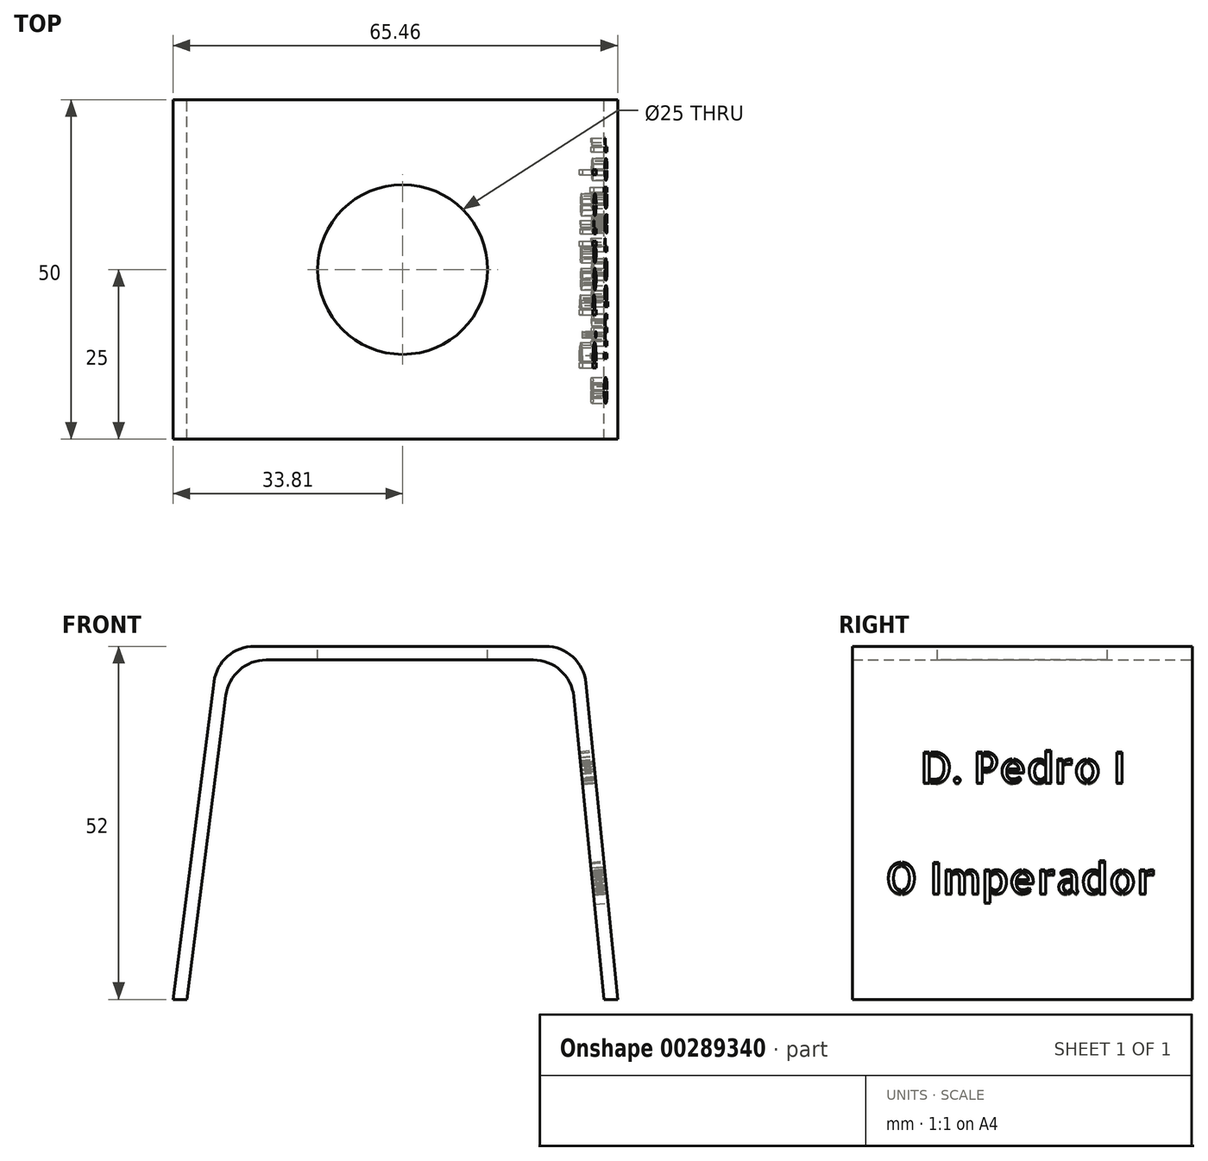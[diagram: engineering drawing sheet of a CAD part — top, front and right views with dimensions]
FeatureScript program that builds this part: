
annotation { "Feature Type Name" : "Feature", "Feature Type Description" : "" }
export const myFeature = defineFeature(function(context is Context, id is Id, definition is map)
    precondition{}
    {
        {
            var Q0;
            Q0=qCreatedBy(makeId("Front.planeOp"),FACE);
            var sketch = newSketch(context, id + "F0", { "sketchPlane" : qUnion([Q0])});
            skPoint(sketch, "E0", {"position": v(0, 0) * mm});
            skLineSegment(sketch, "E1", {"start": v(-31.8, 0) * mm, "end": v(-25.36, 50) * mm});
            skLineSegment(sketch, "E2", {"start": v(24.64, 50) * mm, "end": v(29.64, 0) * mm});
            skLineSegment(sketch, "E3", {"start": v(-25.36, 50) * mm, "end": v(24.64, 50) * mm});
            skLineSegment(sketch, "E4.0", {"start": v(26.45, 52) * mm, "end": v(31.65, 0) * mm});
            skLineSegment(sketch, "E4.1", {"start": v(-27.11, 52) * mm, "end": v(26.45, 52) * mm});
            skLineSegment(sketch, "E4.2", {"start": v(-33.81, 0) * mm, "end": v(-27.11, 52) * mm});
            skLineSegment(sketch, "E5", {"start": v(-33.81, 0) * mm, "end": v(-31.8, 0) * mm});
            skLineSegment(sketch, "E6", {"start": v(29.64, 0) * mm, "end": v(31.65, 0) * mm});
            skSolve(sketch);
        }
        {
            var Q0;
            Q0=makeQuery(id+"F0.imprint","IMPRINT",FACE,{"disambiguationData":[TD([[makeQuery(id+"F0.imprint","IMPRINT",EDGE,{"derivedFrom":sQuery(id+"F0.wireOp",EDGE,"E1")}),1.0]])]});
            var Q1;
            Q1=sQuery(id+"F0.wireOp",EDGE,"E4.2");
            var Q2;
            Q2=sQuery(id+"F0.wireOp",EDGE,"E1");
            extrude(context, id + "F1", {"entities" : qUnion([Q0]), "surfaceEntities" : qUnion([Q1, Q2]), "depth" : 50 * mm});
        }
        {
            var Q0;
            Q0=makeQuery(id+"F1.opExtrude","SWEPT_EDGE",EDGE,{"disambiguationData":[OSD([sQuery(id+"F0.wireOp",EDGE,"E4.0"),sQuery(id+"F0.wireOp",EDGE,"E4.1")])]});
            var Q1;
            Q1=makeQuery(id+"F1.opExtrude","SWEPT_EDGE",EDGE,{"disambiguationData":[OSD([sQuery(id+"F0.wireOp",EDGE,"E4.1"),sQuery(id+"F0.wireOp",EDGE,"E4.2")])]});
            var Q2;
            Q2=makeQuery(id+"F1.opExtrude","SWEPT_EDGE",EDGE,{"disambiguationData":[OSD([sQuery(id+"F0.wireOp",EDGE,"E1"),sQuery(id+"F0.wireOp",EDGE,"E3")])]});
            var Q3;
            Q3=makeQuery(id+"F1.opExtrude","SWEPT_EDGE",EDGE,{"disambiguationData":[OSD([sQuery(id+"F0.wireOp",EDGE,"E2"),sQuery(id+"F0.wireOp",EDGE,"E3")])]});
            fillet(context, id + "F2", {"entities" : qUnion([Q0, Q1, Q2, Q3]), "radius" : 6 * mm, "tangentPropagation" : true});
        }
        {
            var Q0;
            Q0=makeQuery(id+"F1.opExtrude","SWEPT_FACE",FACE,{"disambiguationData":[OSD([sQuery(id+"F0.wireOp",EDGE,"E4.0")])]});
            var sketch = newSketch(context, id + "F3", { "sketchPlane" : qUnion([Q0])});
            skText(sketch, "E7", { "text": "   D. Pedro I\n\nO Imperador", "fontName": "AllertaStencil-Regular.ttf"});
            const initialGuessF3  = {"E7": [-0.04521, 0.02888, 1, 0, 0.00461]};
            skSetInitialGuess(sketch, initialGuessF3);
            skSolve(sketch);
        }
        {
            var Q0;
            Q0=qSketchRegion(id+"F3",true);
            var Q1;
            Q1=makeQuery(id+"F3.imprint","IMPRINT",FACE,{"disambiguationData":[TD([[makeQuery(id+"F3.imprint","IMPRINT",EDGE,{"derivedFrom":sQuery(id+"F3.wireOp",EDGE,"E7.sketch_text.stroke-38")}),-1.0]])]});
            var Q2;
            Q2=makeQuery(id+"F3.imprint","IMPRINT",FACE,{"disambiguationData":[TD([[makeQuery(id+"F3.imprint","IMPRINT",EDGE,{"derivedFrom":sQuery(id+"F3.wireOp",EDGE,"E7.sketch_text.stroke-34")}),-1.0]])]});
            var Q3;
            Q3=makeQuery(id+"F3.imprint","IMPRINT",FACE,{"disambiguationData":[TD([[makeQuery(id+"F3.imprint","IMPRINT",EDGE,{"derivedFrom":sQuery(id+"F3.wireOp",EDGE,"E7.sketch_text.stroke-26")}),-1.0]])]});
            var Q4;
            Q4=makeQuery(id+"F3.imprint","IMPRINT",FACE,{"disambiguationData":[TD([[makeQuery(id+"F3.imprint","IMPRINT",EDGE,{"derivedFrom":sQuery(id+"F3.wireOp",EDGE,"E7.sketch_text.stroke-4")}),-1.0]])]});
            var Q5;
            Q5=makeQuery(id+"F3.imprint","IMPRINT",FACE,{"disambiguationData":[TD([[makeQuery(id+"F3.imprint","IMPRINT",EDGE,{"derivedFrom":sQuery(id+"F3.wireOp",EDGE,"E7.sketch_text.stroke-0")}),-1.0]])]});
            var Q6;
            Q6=makeQuery(id+"F3.imprint","IMPRINT",FACE,{"disambiguationData":[TD([[makeQuery(id+"F3.imprint","IMPRINT",EDGE,{"derivedFrom":sQuery(id+"F3.wireOp",EDGE,"E7.sketch_text.stroke-177")}),-1.0]])]});
            var Q7;
            Q7=makeQuery(id+"F3.imprint","IMPRINT",FACE,{"disambiguationData":[TD([[makeQuery(id+"F3.imprint","IMPRINT",EDGE,{"derivedFrom":sQuery(id+"F3.wireOp",EDGE,"E7.sketch_text.stroke-193")}),-1.0]])]});
            var Q8;
            Q8=makeQuery(id+"F3.imprint","IMPRINT",FACE,{"disambiguationData":[TD([[makeQuery(id+"F3.imprint","IMPRINT",EDGE,{"derivedFrom":sQuery(id+"F3.wireOp",EDGE,"E7.sketch_text.stroke-327")}),-1.0]])]});
            var Q9;
            Q9=makeQuery(id+"F3.imprint","IMPRINT",FACE,{"disambiguationData":[TD([[makeQuery(id+"F3.imprint","IMPRINT",EDGE,{"derivedFrom":sQuery(id+"F3.wireOp",EDGE,"E7.sketch_text.stroke-320")}),-1.0]])]});
            var Q10;
            Q10=makeQuery(id+"F3.imprint","IMPRINT",FACE,{"disambiguationData":[TD([[makeQuery(id+"F3.imprint","IMPRINT",EDGE,{"derivedFrom":sQuery(id+"F3.wireOp",EDGE,"E7.sketch_text.stroke-296")}),-1.0]])]});
            var Q11;
            Q11=makeQuery(id+"F3.imprint","IMPRINT",FACE,{"disambiguationData":[TD([[makeQuery(id+"F3.imprint","IMPRINT",EDGE,{"derivedFrom":sQuery(id+"F3.wireOp",EDGE,"E7.sketch_text.stroke-97")}),-1.0]])]});
            var Q12;
            Q12=makeQuery(id+"F3.imprint","IMPRINT",FACE,{"disambiguationData":[TD([[makeQuery(id+"F3.imprint","IMPRINT",EDGE,{"derivedFrom":sQuery(id+"F3.wireOp",EDGE,"E7.sketch_text.stroke-257")}),-1.0]])]});
            var Q13;
            Q13=makeQuery(id+"F3.imprint","IMPRINT",FACE,{"disambiguationData":[TD([[makeQuery(id+"F3.imprint","IMPRINT",EDGE,{"derivedFrom":sQuery(id+"F3.wireOp",EDGE,"E7.sketch_text.stroke-252")}),-1.0]])]});
            var Q14;
            Q14=makeQuery(id+"F3.imprint","IMPRINT",FACE,{"disambiguationData":[TD([[makeQuery(id+"F3.imprint","IMPRINT",EDGE,{"derivedFrom":sQuery(id+"F3.wireOp",EDGE,"E7.sketch_text.stroke-157")}),-1.0]])]});
            var Q15;
            Q15=makeQuery(id+"F3.imprint","IMPRINT",FACE,{"disambiguationData":[TD([[makeQuery(id+"F3.imprint","IMPRINT",EDGE,{"derivedFrom":sQuery(id+"F3.wireOp",EDGE,"E7.sketch_text.stroke-60")}),-1.0]])]});
            var Q16;
            Q16=makeQuery(id+"F3.imprint","IMPRINT",FACE,{"disambiguationData":[TD([[makeQuery(id+"F3.imprint","IMPRINT",EDGE,{"derivedFrom":sQuery(id+"F3.wireOp",EDGE,"E7.sketch_text.stroke-234")}),-1.0]])]});
            var Q17;
            Q17=makeQuery(id+"F3.imprint","IMPRINT",FACE,{"disambiguationData":[TD([[makeQuery(id+"F3.imprint","IMPRINT",EDGE,{"derivedFrom":sQuery(id+"F3.wireOp",EDGE,"E7.sketch_text.stroke-141")}),-1.0]])]});
            var Q18;
            Q18=makeQuery(id+"F3.imprint","IMPRINT",FACE,{"disambiguationData":[TD([[makeQuery(id+"F3.imprint","IMPRINT",EDGE,{"derivedFrom":sQuery(id+"F3.wireOp",EDGE,"E7.sketch_text.stroke-218")}),-1.0]])]});
            var Q19;
            Q19=makeQuery(id+"F3.imprint","IMPRINT",FACE,{"disambiguationData":[TD([[makeQuery(id+"F3.imprint","IMPRINT",EDGE,{"derivedFrom":sQuery(id+"F3.wireOp",EDGE,"E7.sketch_text.stroke-458")}),-1.0]])]});
            var Q20;
            Q20=makeQuery(id+"F3.imprint","IMPRINT",FACE,{"disambiguationData":[TD([[makeQuery(id+"F3.imprint","IMPRINT",EDGE,{"derivedFrom":sQuery(id+"F3.wireOp",EDGE,"E7.sketch_text.stroke-394")}),-1.0]])]});
            var Q21;
            Q21=makeQuery(id+"F3.imprint","IMPRINT",FACE,{"disambiguationData":[TD([[makeQuery(id+"F3.imprint","IMPRINT",EDGE,{"derivedFrom":sQuery(id+"F3.wireOp",EDGE,"E7.sketch_text.stroke-435")}),-1.0]])]});
            var Q22;
            Q22=makeQuery(id+"F3.imprint","IMPRINT",FACE,{"disambiguationData":[TD([[makeQuery(id+"F3.imprint","IMPRINT",EDGE,{"derivedFrom":sQuery(id+"F3.wireOp",EDGE,"E7.sketch_text.stroke-73")}),-1.0]])]});
            var Q23;
            Q23=makeQuery(id+"F3.imprint","IMPRINT",FACE,{"disambiguationData":[TD([[makeQuery(id+"F3.imprint","IMPRINT",EDGE,{"derivedFrom":sQuery(id+"F3.wireOp",EDGE,"E7.sketch_text.stroke-389")}),-1.0]])]});
            var Q24;
            Q24=makeQuery(id+"F3.imprint","IMPRINT",FACE,{"disambiguationData":[TD([[makeQuery(id+"F3.imprint","IMPRINT",EDGE,{"derivedFrom":sQuery(id+"F3.wireOp",EDGE,"E7.sketch_text.stroke-102")}),-1.0]])]});
            var Q25;
            Q25=makeQuery(id+"F3.imprint","IMPRINT",FACE,{"disambiguationData":[TD([[makeQuery(id+"F3.imprint","IMPRINT",EDGE,{"derivedFrom":sQuery(id+"F3.wireOp",EDGE,"E7.sketch_text.stroke-127")}),-1.0]])]});
            var Q26;
            Q26=makeQuery(id+"F3.imprint","IMPRINT",FACE,{"disambiguationData":[TD([[makeQuery(id+"F3.imprint","IMPRINT",EDGE,{"derivedFrom":sQuery(id+"F3.wireOp",EDGE,"E7.sketch_text.stroke-173")}),-1.0]])]});
            var Q27;
            Q27=makeQuery(id+"F3.imprint","IMPRINT",FACE,{"disambiguationData":[TD([[makeQuery(id+"F3.imprint","IMPRINT",EDGE,{"derivedFrom":sQuery(id+"F3.wireOp",EDGE,"E7.sketch_text.stroke-283")}),-1.0]])]});
            var Q28;
            Q28=makeQuery(id+"F3.imprint","IMPRINT",FACE,{"disambiguationData":[TD([[makeQuery(id+"F3.imprint","IMPRINT",EDGE,{"derivedFrom":sQuery(id+"F3.wireOp",EDGE,"E7.sketch_text.stroke-353")}),-1.0]])]});
            var Q29;
            Q29=makeQuery(id+"F3.imprint","IMPRINT",FACE,{"disambiguationData":[TD([[makeQuery(id+"F3.imprint","IMPRINT",EDGE,{"derivedFrom":sQuery(id+"F3.wireOp",EDGE,"E7.sketch_text.stroke-334")}),-1.0]])]});
            var Q30;
            Q30=makeQuery(id+"F3.imprint","IMPRINT",FACE,{"disambiguationData":[TD([[makeQuery(id+"F3.imprint","IMPRINT",EDGE,{"derivedFrom":sQuery(id+"F3.wireOp",EDGE,"E7.sketch_text.stroke-213")}),-1.0]])]});
            var Q31;
            Q31=makeQuery(id+"F3.imprint","IMPRINT",FACE,{"disambiguationData":[TD([[makeQuery(id+"F3.imprint","IMPRINT",EDGE,{"derivedFrom":sQuery(id+"F3.wireOp",EDGE,"E7.sketch_text.stroke-451")}),-1.0]])]});
            var Q32;
            Q32=makeQuery(id+"F3.imprint","IMPRINT",FACE,{"disambiguationData":[TD([[makeQuery(id+"F3.imprint","IMPRINT",EDGE,{"derivedFrom":sQuery(id+"F3.wireOp",EDGE,"E7.sketch_text.stroke-209")}),-1.0]])]});
            var Q33;
            Q33=makeQuery(id+"F3.imprint","IMPRINT",FACE,{"disambiguationData":[TD([[makeQuery(id+"F3.imprint","IMPRINT",EDGE,{"derivedFrom":sQuery(id+"F3.wireOp",EDGE,"E7.sketch_text.stroke-419")}),-1.0]])]});
            var Q34;
            Q34=makeQuery(id+"F3.imprint","IMPRINT",FACE,{"disambiguationData":[TD([[makeQuery(id+"F3.imprint","IMPRINT",EDGE,{"derivedFrom":sQuery(id+"F3.wireOp",EDGE,"E7.sketch_text.stroke-134")}),-1.0]])]});
            extrude(context, id + "F4", {"entities" : qUnion([Q0, Q1, Q2, Q3, Q4, Q5, Q6, Q7, Q8, Q9, Q10, Q11, Q12, Q13, Q14, Q15, Q16, Q17, Q18, Q19, Q20, Q21, Q22, Q23, Q24, Q25, Q26, Q27, Q28, Q29, Q30, Q31, Q32, Q33, Q34]), "operationType" : NewBodyOperationType.REMOVE, "oppositeDirection" : true, "depth" : 2 * mm});
        }
        {
            var Q0;
            Q0=makeQuery(id+"F1.opExtrude","SWEPT_FACE",FACE,{"disambiguationData":[OSD([sQuery(id+"F0.wireOp",EDGE,"E4.1")])]});
            var sketch = newSketch(context, id + "F5", { "sketchPlane" : qUnion([Q0])});
            skPoint(sketch, "E8", {"position": v(0, -25) * mm});
            skLineSegment(sketch, "E9", {"start": v(0, 0) * mm, "end": v(0, -50) * mm, "construction": true});
            skCircle(sketch, "E10", {"center": v(0, -25) * mm, "radius": 12.5 * mm});
            skSolve(sketch);
        }
        {
            var Q0;
            Q0=makeQuery(id+"F5.imprint","IMPRINT",FACE,{"disambiguationData":[TD([[makeQuery(id+"F5.imprint","IMPRINT",EDGE,{"derivedFrom":sQuery(id+"F5.wireOp",EDGE,"E10")}),1.0]])]});
            extrude(context, id + "F6", {"entities" : qUnion([Q0]), "operationType" : NewBodyOperationType.REMOVE, "oppositeDirection" : true, "depth" : 2 * mm});
        }
    });
